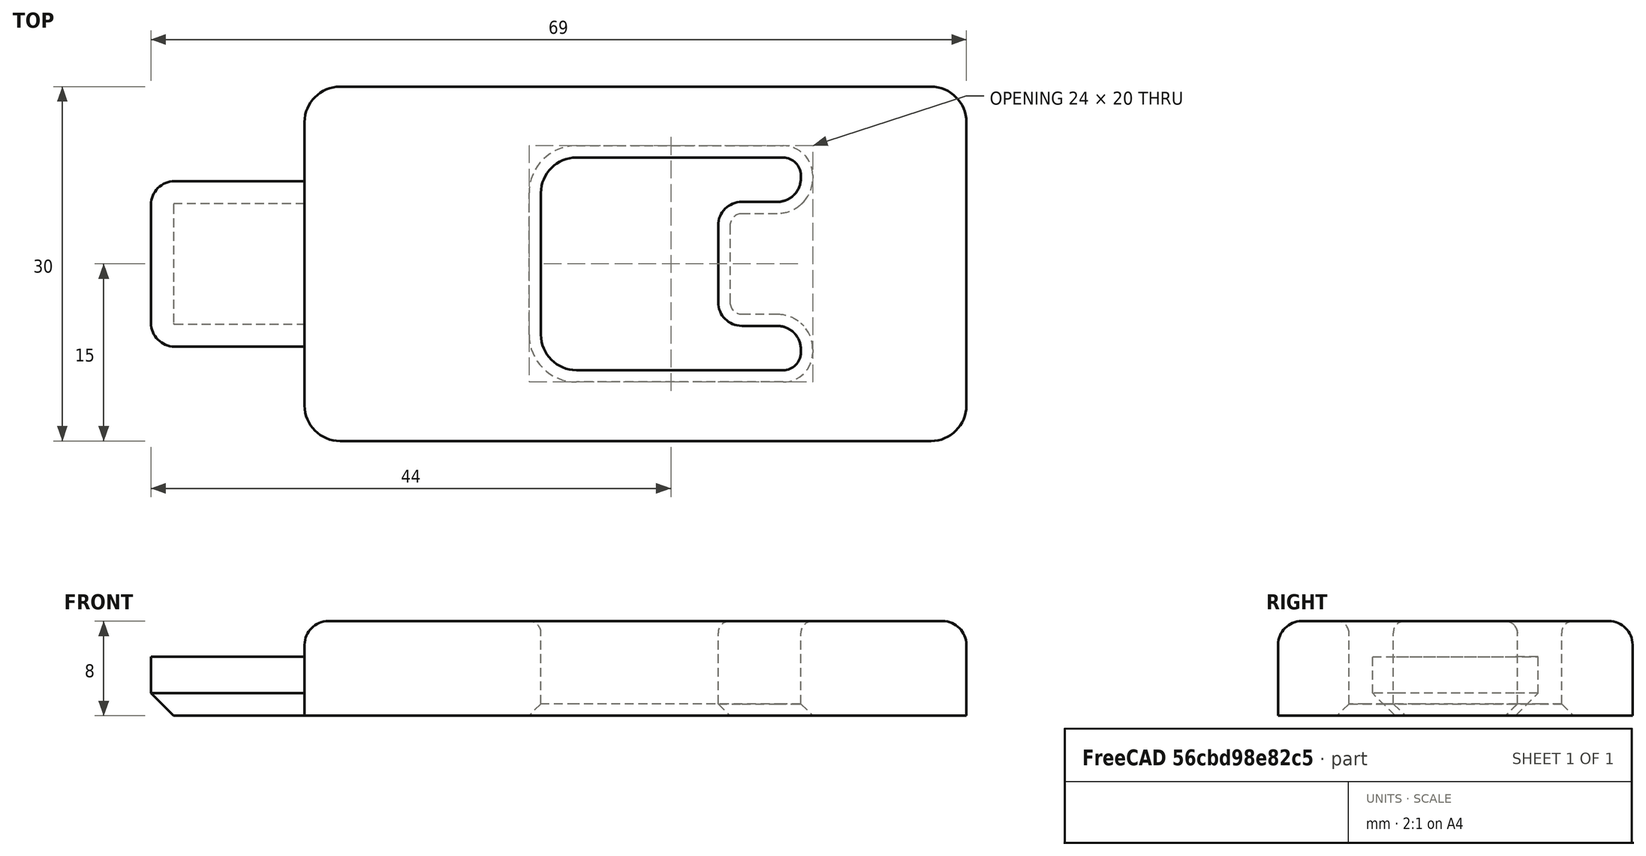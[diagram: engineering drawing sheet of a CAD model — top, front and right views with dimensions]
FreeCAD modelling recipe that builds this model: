
FCSTD DOCUMENT  (FreeCAD 0.17R13541 (Git))
Label: reel-clamp
License: All rights reserved
LicenseURL: http://en.wikipedia.org/wiki/All_rights_reserved
objects: Part::Fillet×7, Part::Box×4, Part::Chamfer×2, Part::Cut×1, Part::MultiFuse×1
note: 15 computed .brp shape members not serialized (recipe doc carries the construction recipe); baked Part::Feature solids carry a one-line shape summary decoded from their .brp

FEATURE [Part::Box] Box  label="Cube"
  AttacherType = Attacher::AttachEngine3D
  Height = 8
  Length = 56
  Placement = pos=(-28,-15,0) rot=(0,0,1;0rad)
  Width = 30
FEATURE [Part::Box] Box001  label="Cube001"
  AttacherType = Attacher::AttachEngine3D
  Height = 14
  Length = 22
  Placement = pos=(-8,-9,-1) rot=(0,0,1;0rad)
  Width = 18
FEATURE [Part::Cut] Cut
  Base = -> Box
  Tool = -> Box001
FEATURE [Part::Box] Box002  label="Cube002"
  AttacherType = Attacher::AttachEngine3D
  Height = 8
  Length = 8
  Placement = pos=(7,-5.25,0) rot=(0,0,1;0rad)
  Width = 10.5
FEATURE [Part::Box] Box003  label="Cube003"
  AttacherType = Attacher::AttachEngine3D
  Height = 5
  Length = 13
  Placement = pos=(-41,-7,0) rot=(0,0,1;0rad)
  Width = 14
FEATURE [Part::MultiFuse] Fusion
  Shapes = -> [Cut,Box002,Box003]
FEATURE [Part::Fillet] Fillet
  Base = -> Fusion
  Edges = 4 edges r=2: [Edge1,Edge3,Edge6,Edge11]
FEATURE [Part::Fillet] Fillet001
  Base = -> Fillet
  Edges = 2 edges r=1.5: [Edge55,Edge58]
FEATURE [Part::Fillet] Fillet002
  Base = -> Fillet001
  Edges = 2 edges r=3: [Edge26,Edge34]
FEATURE [Part::Fillet] Fillet003
  Base = -> Fillet002
  Edges = 14 edges r=1: [Edge1,Edge2,Edge3,Edge4,Edge6,Edge7,Edge8,Edge10,Edge14,Edge38,Edge39,Edge40,Edge42,Edge43]
FEATURE [Part::Chamfer] Chamfer
  Base = -> Fillet003
  Edges = 14 edges r=1: [Edge70,Edge74,Edge78,Edge81,Edge84,Edge87,Edge88,Edge91,Edge92,Edge118,Edge120,Edge121,Edge122,Edge124]
FEATURE [Part::Fillet] Fillet004
  Base = -> Chamfer
  Edges = 4 edges r=3: [Edge130,Edge134,Edge135,Edge139]
FEATURE [Part::Fillet] Fillet005
  Base = -> Fillet004
  Edges = 8 edges r=2: [Edge25,Edge32,Edge37,Edge39,Edge41,Edge42,Edge45,Edge46]
FEATURE [Part::Fillet] Fillet006
  Base = -> Fillet005
  Edges = 2 edges r=2: [Edge40,Edge44]
FEATURE [Part::Chamfer] Chamfer001
  Base = -> Fillet006
  Edges = 5 edges r=1.9: [Edge1,Edge5,Edge6,Edge7,Edge8]
